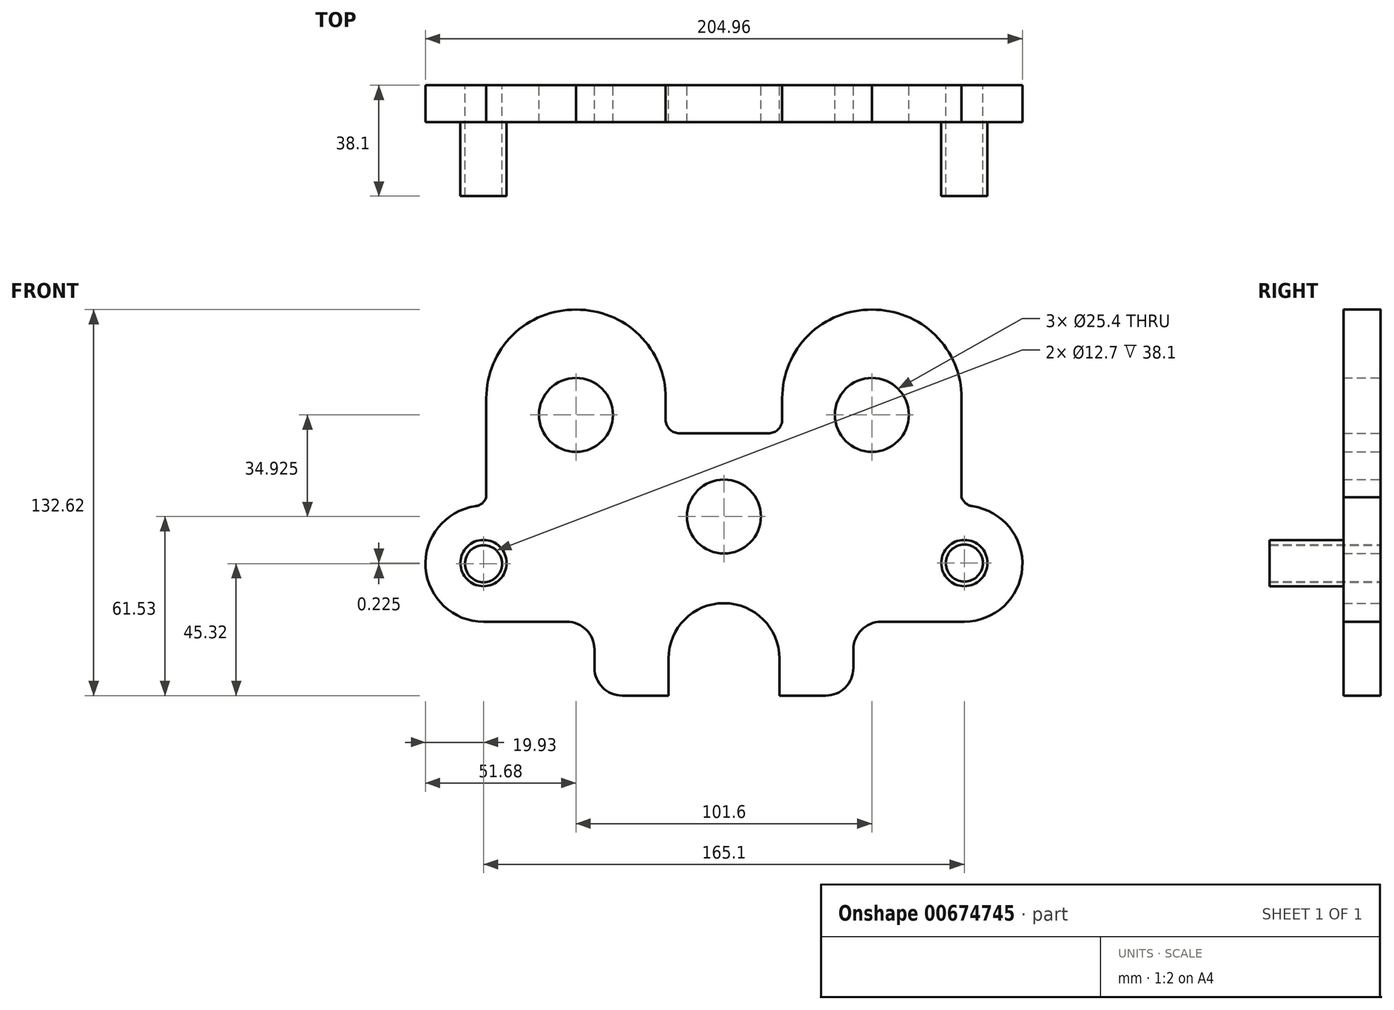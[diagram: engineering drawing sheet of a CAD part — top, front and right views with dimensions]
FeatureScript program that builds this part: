
annotation { "Feature Type Name" : "Feature", "Feature Type Description" : "" }
export const myFeature = defineFeature(function(context is Context, id is Id, definition is map)
    precondition{}
    {
        {
            var Q0;
            Q0=qCreatedBy(makeId("Front.planeOp"),FACE);
            var sketch = newSketch(context, id + "F0", { "sketchPlane" : qUnion([Q0])});
            skCircle(sketch, "E0", {"center": v(0, 0) * mm, "radius": 12.7 * mm});
            skCircle(sketch, "E1", {"center": v(-50.8, 34.92) * mm, "radius": 12.7 * mm});
            skCircle(sketch, "E2", {"center": v(50.8, 34.93) * mm, "radius": 12.7 * mm});
            skCircle(sketch, "E3", {"center": v(-82.55, -16.21) * mm, "radius": 6.35 * mm});
            skCircle(sketch, "E4", {"center": v(82.55, -15.99) * mm, "radius": 6.35 * mm});
            skLineSegment(sketch, "E5", {"start": v(-50.8, 34.92) * mm, "end": v(-50.8, 71.09) * mm, "construction": true});
            skLineSegment(sketch, "E6", {"start": v(50.8, 34.93) * mm, "end": v(104.97, 34.93) * mm, "construction": true});
            skPoint(sketch, "E7", {"position": v(77.89, 34.93) * mm});
            skLineSegment(sketch, "E8", {"start": v(-82.55, -16.21) * mm, "end": v(-82.55, 0) * mm, "construction": true});
            skArc(sketch, "E9", {"start": v(-85.38, 3.52) * mm, "mid": v(-102.43, -17.63) * mm, "end": v(-82.55, -36.14) * mm});
            skLineSegment(sketch, "E10", {"start": v(-82.55, -36.14) * mm, "end": v(-82.55, -36.14) * mm});
            skArc(sketch, "E11.MirrorCS", {"start": v(85.38, 3.52) * mm, "mid": v(102.43, -17.63) * mm, "end": v(82.55, -36.14) * mm});
            skLineSegment(sketch, "E12.MirrorCS", {"start": v(82.55, -36.14) * mm, "end": v(82.55, -36.14) * mm});
            skLineSegment(sketch, "E13", {"start": v(-82.55, -36.14) * mm, "end": v(-53.98, -36.14) * mm});
            skLineSegment(sketch, "E14.MirrorCS", {"start": v(82.55, -36.14) * mm, "end": v(53.98, -36.14) * mm});
            skArc(sketch, "E15", {"start": v(-50.8, 71.09) * mm, "mid": v(-29.05, 62.34) * mm, "end": v(-20, 40.71) * mm});
            skArc(sketch, "E16.MirrorCS", {"start": v(50.8, 71.09) * mm, "mid": v(29.05, 62.34) * mm, "end": v(20, 40.71) * mm});
            skLineSegment(sketch, "E17", {"start": v(-82.55, 3.72) * mm, "end": v(-82.55, 3.72) * mm});
            skLineSegment(sketch, "E18.MirrorCS", {"start": v(82.55, 3.72) * mm, "end": v(82.55, 3.72) * mm});
            skLineSegment(sketch, "E19", {"start": v(-20, 40.71) * mm, "end": v(-20, 33.34) * mm});
            skLineSegment(sketch, "E20.MirrorCS", {"start": v(20, 40.71) * mm, "end": v(20, 33.34) * mm});
            skLineSegment(sketch, "E21", {"start": v(-15.25, 28.58) * mm, "end": v(15.25, 28.58) * mm});
            skLineSegment(sketch, "E22", {"start": v(-34.93, -61.53) * mm, "end": v(-19.05, -61.53) * mm});
            skLineSegment(sketch, "E23", {"start": v(-19.05, -48.83) * mm, "end": v(-19.05, -61.53) * mm});
            skLineSegment(sketch, "E24.MirrorCS", {"start": v(19.05, -48.83) * mm, "end": v(19.05, -61.53) * mm});
            skLineSegment(sketch, "E25.MirrorCS", {"start": v(34.93, -61.53) * mm, "end": v(19.05, -61.53) * mm});
            skArc(sketch, "E26", {"start": v(-19.05, -48.83) * mm, "mid": v(-13.47, -35.36) * mm, "end": v(0, -29.78) * mm});
            skArc(sketch, "E27.MirrorCS", {"start": v(19.05, -48.83) * mm, "mid": v(13.47, -35.36) * mm, "end": v(0, -29.78) * mm});
            skLineSegment(sketch, "E28", {"start": v(-44.45, -44.96) * mm, "end": v(-44.45, -45.67) * mm});
            skLineSegment(sketch, "E29", {"start": v(-44.45, -44.96) * mm, "end": v(-44.45, -52) * mm});
            skLineSegment(sketch, "E30.MirrorCS", {"start": v(44.45, -44.96) * mm, "end": v(44.45, -45.67) * mm});
            skLineSegment(sketch, "E31.MirrorCS", {"start": v(44.45, -44.96) * mm, "end": v(44.45, -52) * mm});
            skPoint(sketch, "E32.visualSharp", {"position": v(-20, 28.57) * mm});
            skArc(sketch, "E32.filletArc", {"start": v(-20, 33.34) * mm, "mid": v(-18.61, 29.97) * mm, "end": v(-15.25, 28.57) * mm});
            skPoint(sketch, "E33.visualSharp", {"position": v(20, 28.57) * mm});
            skArc(sketch, "E33.filletArc", {"start": v(15.25, 28.57) * mm, "mid": v(18.61, 29.97) * mm, "end": v(20, 33.34) * mm});
            skPoint(sketch, "E34.visualSharp", {"position": v(-82.55, 3.72) * mm});
            skArc(sketch, "E34.filletArc", {"start": v(-85.38, 3.52) * mm, "mid": v(-83.07, 4.53) * mm, "end": v(-81.6, 6.58) * mm});
            skPoint(sketch, "E35.visualSharp", {"position": v(82.55, 3.72) * mm});
            skArc(sketch, "E35.filletArc", {"start": v(81.6, 6.57) * mm, "mid": v(83.07, 4.52) * mm, "end": v(85.38, 3.52) * mm});
            skPoint(sketch, "E36.visualSharp", {"position": v(-44.45, -61.53) * mm});
            skArc(sketch, "E36.filletArc", {"start": v(-44.45, -52) * mm, "mid": v(-41.66, -58.74) * mm, "end": v(-34.93, -61.53) * mm});
            skPoint(sketch, "E37.visualSharp", {"position": v(44.45, -61.53) * mm});
            skArc(sketch, "E37.filletArc", {"start": v(34.93, -61.53) * mm, "mid": v(41.66, -58.74) * mm, "end": v(44.45, -52) * mm});
            skPoint(sketch, "E38.visualSharp", {"position": v(-44.45, -36.14) * mm});
            skArc(sketch, "E38.filletArc", {"start": v(-44.45, -45.67) * mm, "mid": v(-47.24, -38.93) * mm, "end": v(-53.98, -36.14) * mm});
            skPoint(sketch, "E39.visualSharp", {"position": v(44.45, -36.14) * mm});
            skArc(sketch, "E39.filletArc", {"start": v(53.98, -36.14) * mm, "mid": v(47.24, -38.93) * mm, "end": v(44.45, -45.67) * mm});
            skArc(sketch, "E40.MirrorCS", {"start": v(-50.8, 71.09) * mm, "mid": v(-72.55, 62.34) * mm, "end": v(-81.6, 40.71) * mm});
            skLineSegment(sketch, "E41", {"start": v(-81.6, 40.71) * mm, "end": v(-81.6, 6.58) * mm});
            skArc(sketch, "E42.MirrorCS", {"start": v(50.8, 71.09) * mm, "mid": v(72.55, 62.34) * mm, "end": v(81.6, 40.71) * mm});
            skLineSegment(sketch, "E43", {"start": v(81.6, 40.71) * mm, "end": v(81.6, 6.57) * mm});
            skCircle(sketch, "E44", {"center": v(82.55, -15.99) * mm, "radius": 7.94 * mm});
            skCircle(sketch, "E45", {"center": v(-82.55, -15.99) * mm, "radius": 7.94 * mm});
            skSolve(sketch);
        }
        {
            var Q0;
            Q0=qSketchRegion(id+"F0",true);
            var Q1;
            Q1=makeQuery(id+"F0.imprint","IMPRINT",FACE,{"disambiguationData":[TD([[makeQuery(id+"F0.imprint","IMPRINT",EDGE,{"derivedFrom":sQuery(id+"F0.wireOp",EDGE,"E3")}),-1.0]])]});
            var Q2;
            Q2=makeQuery(id+"F0.imprint","IMPRINT",FACE,{"disambiguationData":[TD([[makeQuery(id+"F0.imprint","IMPRINT",EDGE,{"derivedFrom":sQuery(id+"F0.wireOp",EDGE,"E4")}),-1.0]])]});
            extrude(context, id + "F1", {"entities" : qUnion([Q0, Q1, Q2]), "depth" : 12.7 * mm, "offsetDistance" : 25.4 * mm});
        }
        {
            var Q0;
            Q0=makeQuery(id+"F0.imprint","IMPRINT",FACE,{"disambiguationData":[TD([[makeQuery(id+"F0.imprint","IMPRINT",EDGE,{"derivedFrom":sQuery(id+"F0.wireOp",EDGE,"E4")}),-1.0]])]});
            var Q1;
            Q1=makeQuery(id+"F0.imprint","IMPRINT",FACE,{"disambiguationData":[TD([[makeQuery(id+"F0.imprint","IMPRINT",EDGE,{"derivedFrom":sQuery(id+"F0.wireOp",EDGE,"E3")}),-1.0]])]});
            extrude(context, id + "F2", {"entities" : qUnion([Q0, Q1]), "operationType" : NewBodyOperationType.ADD, "depth" : 38.1 * mm, "offsetDistance" : 25.4 * mm});
        }
    });
